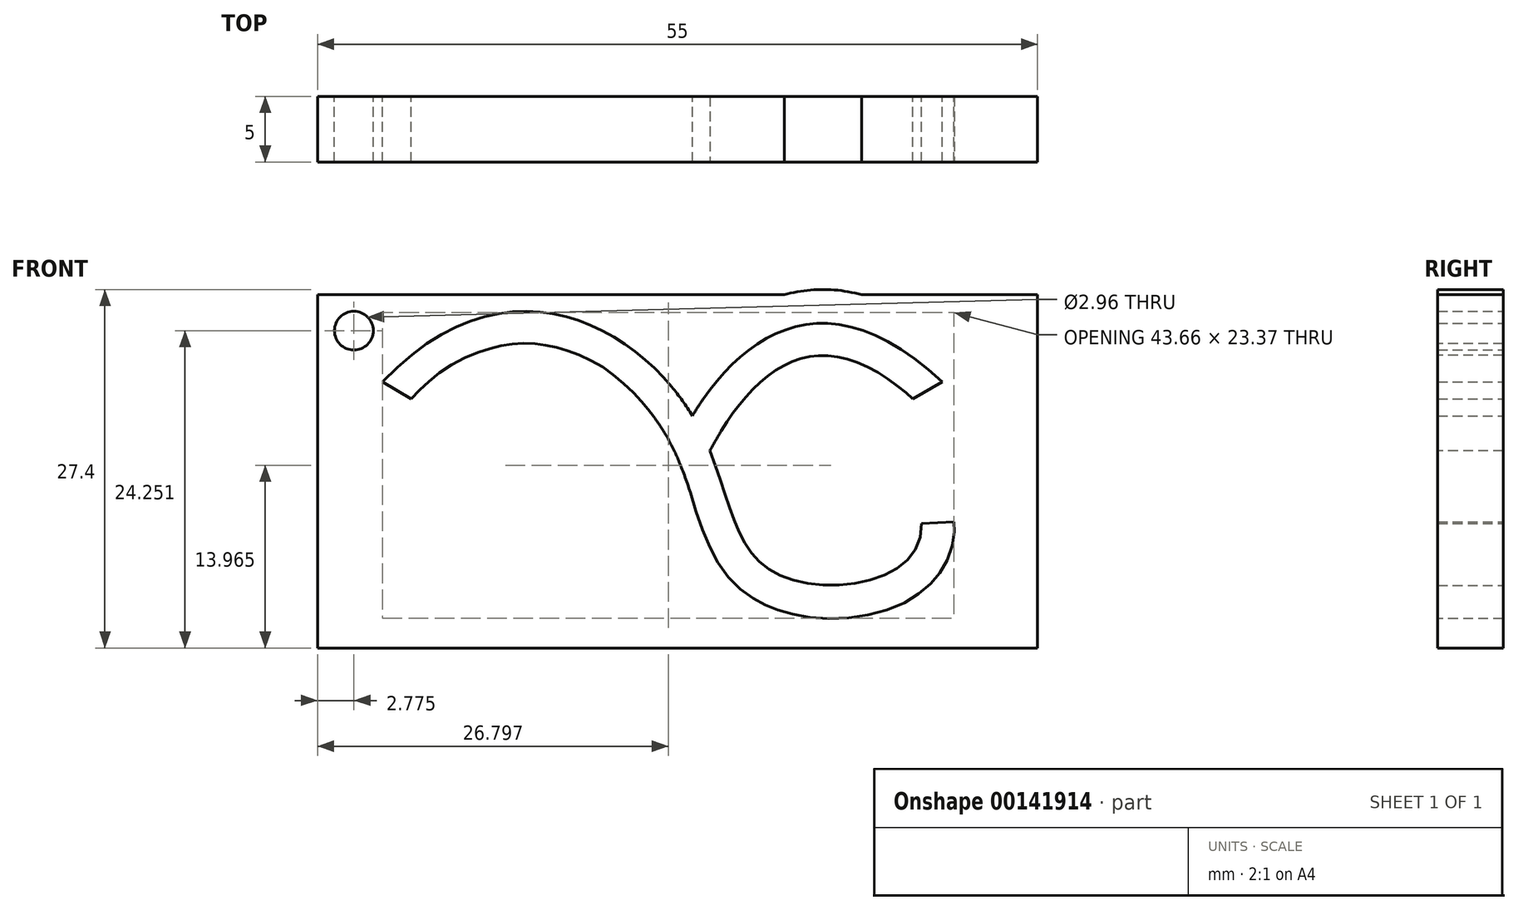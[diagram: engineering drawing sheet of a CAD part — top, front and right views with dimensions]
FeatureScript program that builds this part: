
annotation { "Feature Type Name" : "Feature", "Feature Type Description" : "" }
export const myFeature = defineFeature(function(context is Context, id is Id, definition is map)
    precondition{}
    {
        {
            var Q0;
            Q0=qCreatedBy(makeId("Front.planeOp"),FACE);
            var sketch = newSketch(context, id + "F0", { "sketchPlane" : qUnion([Q0])});
            skLineSegment(sketch, "E0.top", {"start": v(0, 35) * mm, "end": v(-55, 35) * mm});
            skLineSegment(sketch, "E0.left", {"start": v(0, 8) * mm, "end": v(0, 35) * mm});
            skLineSegment(sketch, "E0.right", {"start": v(-55, 8) * mm, "end": v(-55, 35) * mm});
            skPoint(sketch, "E1", {"position": v(-26.36, 25.75) * mm});
            skPoint(sketch, "E2", {"position": v(-7.29, 28.35) * mm});
            skPoint(sketch, "E3", {"position": v(-50.04, 28.35) * mm});
            skLineSegment(sketch, "E4", {"start": v(-55, 10.48) * mm, "end": v(-55, 35) * mm});
            skPoint(sketch, "E5", {"position": v(-48.86, 21.39) * mm});
            skPoint(sketch, "E6", {"position": v(-36, 11.39) * mm});
            skPoint(sketch, "E7", {"position": v(-19.78, 13.6) * mm});
            skFitSpline(sketch, "E8", {"points": [v(-50.04, 28.35) * mm, v(-26.36, 25.75) * mm, v(-19.78, 13.6) * mm, v(-8.87, 17.52) * mm], "startDerivative": vector(71.85, 74.98) * mm, "endDerivative": vector(-2.39, 49.12) * mm});
            skFitSpline(sketch, "E9", {"points": [v(-48.86, 21.39) * mm, v(-36, 11.39) * mm, v(-26.36, 25.75) * mm, v(-7.29, 28.35) * mm], "startDerivative": vector(-9.22, -77.23) * mm, "endDerivative": vector(76.85, -71.86) * mm});
            skLineSegment(sketch, "E10", {"start": v(-41.15, 21.2) * mm, "end": v(-48.86, 21.39) * mm});
            skPoint(sketch, "E11", {"position": v(-36.8, 21.2) * mm});
            skLineSegment(sketch, "E12", {"start": v(-36.8, 21.2) * mm, "end": v(-41.15, 21.2) * mm});
            skFitSpline(sketch, "E13.0", {"points": [v(-48.23, 26.62) * mm, v(-46.88, 28.03) * mm, v(-44.9, 29.56) * mm, v(-42.47, 30.68) * mm, v(-40.73, 31.14) * mm, v(-39.06, 31.28) * mm, v(-37.45, 31.13) * mm, v(-35.9, 30.72) * mm, v(-33.88, 29.85) * mm, v(-32.02, 28.57) * mm, v(-30.4, 27.02) * mm, v(-29.53, 25.97) * mm, v(-28.92, 25.11) * mm, v(-28.5, 24.47) * mm, v(-28.13, 23.82) * mm, v(-27.7, 22.95) * mm, v(-27.21, 21.82) * mm, v(-26.55, 19.99) * mm, v(-25.98, 18.1) * mm, v(-25.26, 16.21) * mm, v(-24.57, 14.8) * mm, v(-23.64, 13.42) * mm, v(-22.58, 12.39) * mm, v(-21.56, 11.7) * mm, v(-20.72, 11.26) * mm, v(-19.84, 10.91) * mm, v(-18.62, 10.56) * mm, v(-17.02, 10.3) * mm, v(-15.06, 10.26) * mm, v(-13.09, 10.5) * mm, v(-11.16, 11.02) * mm, v(-9.65, 11.75) * mm, v(-8.54, 12.58) * mm, v(-7.78, 13.34) * mm, v(-7.14, 14.24) * mm, v(-6.66, 15.3) * mm, v(-6.38, 16.44) * mm, v(-6.35, 17.24) * mm, v(-6.37, 17.65) * mm]});
            skFitSpline(sketch, "E14.0", {"points": [v(-51.34, 21.68) * mm, v(-51.46, 20.7) * mm, v(-51.47, 18.8) * mm, v(-50.85, 16.2) * mm, v(-49.69, 13.95) * mm, v(-48.11, 12.1) * mm, v(-46.26, 10.66) * mm, v(-44.23, 9.6) * mm, v(-42.1, 8.88) * mm, v(-39.95, 8.5) * mm, v(-37.8, 8.47) * mm, v(-36.08, 8.73) * mm, v(-34.76, 9.15) * mm, v(-33.52, 9.7) * mm, v(-32.15, 10.62) * mm, v(-30.8, 11.95) * mm, v(-29.7, 13.43) * mm, v(-28.78, 15) * mm, v(-27.7, 17.17) * mm, v(-26.73, 19.4) * mm, v(-25.74, 21.6) * mm, v(-24.95, 23.2) * mm, v(-24.1, 24.7) * mm, v(-23.13, 26.13) * mm, v(-22.08, 27.4) * mm, v(-20.96, 28.5) * mm, v(-19.8, 29.35) * mm, v(-18.6, 29.94) * mm, v(-17.39, 30.28) * mm, v(-16.1, 30.35) * mm, v(-14.66, 30.12) * mm, v(-13, 29.49) * mm, v(-11.12, 28.35) * mm, v(-9.72, 27.2) * mm, v(-9, 26.53) * mm]});
            skFitSpline(sketch, "E15.0", {"points": [v(-46.37, 21.09) * mm, v(-46.45, 20.46) * mm, v(-46.45, 19.33) * mm, v(-46.11, 17.95) * mm, v(-45.5, 16.77) * mm, v(-44.64, 15.75) * mm, v(-43.55, 14.89) * mm, v(-42.26, 14.21) * mm, v(-40.87, 13.74) * mm, v(-39.46, 13.5) * mm, v(-38.13, 13.48) * mm, v(-37.17, 13.64) * mm, v(-36.54, 13.84) * mm, v(-35.98, 14.09) * mm, v(-35.35, 14.5) * mm, v(-34.61, 15.22) * mm, v(-33.9, 16.18) * mm, v(-33.19, 17.36) * mm, v(-32.26, 19.21) * mm, v(-31.33, 21.38) * mm, v(-30.27, 23.72) * mm, v(-29.38, 25.52) * mm, v(-28.35, 27.33) * mm, v(-27.16, 29.1) * mm, v(-25.79, 30.78) * mm, v(-24.22, 32.3) * mm, v(-22.45, 33.61) * mm, v(-20.44, 34.63) * mm, v(-18.2, 35.25) * mm, v(-15.8, 35.38) * mm, v(-13.28, 34.96) * mm, v(-10.74, 33.97) * mm, v(-8.18, 32.42) * mm, v(-6.45, 31) * mm, v(-5.58, 30.18) * mm]});
            skLineSegment(sketch, "E15.1", {"start": v(-41.18, 18.7) * mm, "end": v(-46.3, 18.82) * mm});
            skLineSegment(sketch, "E15.2", {"start": v(-36.8, 18.7) * mm, "end": v(-41.18, 18.7) * mm});
            skLineSegment(sketch, "E16", {"start": v(-7.29, 28.35) * mm, "end": v(-9.53, 27.01) * mm});
            skLineSegment(sketch, "E17", {"start": v(-8.87, 17.52) * mm, "end": v(-6.37, 17.65) * mm});
            skLineSegment(sketch, "E18", {"start": v(-50.04, 28.35) * mm, "end": v(-47.84, 27.02) * mm});
            skLineSegment(sketch, "E19", {"start": v(-36.8, 18.7) * mm, "end": v(-36.8, 21.2) * mm});
            skLineSegment(sketch, "E20", {"start": v(-55, 8) * mm, "end": v(0, 8) * mm});
            skCircle(sketch, "E21", {"center": v(-52.23, 32.25) * mm, "radius": 1.48 * mm});
            skLineSegment(sketch, "E22", {"start": v(-36.8, 21.2) * mm, "end": v(-36.8, 18.7) * mm});
            skLineSegment(sketch, "E23", {"start": v(-24.14, 24.58) * mm, "end": v(-25.52, 27.04) * mm});
            skLineSegment(sketch, "E24", {"start": v(-29.91, 24.44) * mm, "end": v(-28.3, 21.99) * mm});
            skSolve(sketch);
        }
        {
            var Q0;
            Q0 = qSketchRegion(id + "F0", true);
            extrude(context, id + "F1", {"entities" : qUnion([Q0]), "endBound" : BoundingType.SYMMETRIC, "depth" : 5 * mm});
        }
    });
